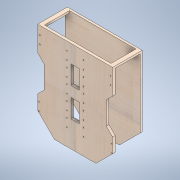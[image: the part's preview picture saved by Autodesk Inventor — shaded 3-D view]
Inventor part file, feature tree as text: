
AUTODESK INVENTOR PART (.ipt)
format: ipt  version: 2021 (Build 250183000, 183)  size: 348,672 bytes
history: native  units: mm
features: extrude x11, sketch x11, other x1, chamfer x1
ambient origin geometry x8: Origin, YZ Plane, XZ Plane, XY Plane, X Axis, Y Axis, Z Axis, Center Point
bodies: Body1 (feature_tree), Body2 (feature_tree)
feature tree (24):
  other  "Sólido1"
  extrude  "Extrusión1"  Depth=120.0mm
  extrude  "Extrusión2"  Depth=180.0mm
  extrude  "Extrusión3"  Depth=100.0mm
  extrude  "Extrusión4"  Depth=12.55mm TaperAngle=0.0deg
  extrude  "Extrusión6"  Depth=30.0mm
  extrude  "Extrusión7"  Depth=30.0mm
  extrude  "Extrusión8"  Depth=10.0mm
  extrude  "Extrusión9"  Depth=5.0mm
  extrude  "Extrusión10"  Depth=19.5mm
  extrude  "Extrusión11"  Depth=40.0mm
  chamfer  "Chaflán1"  Distance=19.5mm
  extrude  "Extrusión12"  Depth=125.0mm
  sketch  "Boceto1"  dims[d0=120.0mm d1=70.0mm]
  sketch  "Boceto2"  dims[d2=110.0mm d3=180.0mm]
  sketch  "Boceto3"  dims[d8=100.0mm d9=80.0mm]
  sketch  "Boceto4"  dims[d13=150.0mm d14=12.55mm d15=0.0mm]
  sketch  "Boceto6"  dims[d17=80.0mm d18=30.0mm]
  sketch  "Boceto7"  dims[d19=30.0mm d20=60.0mm]
  sketch  "Boceto8"  dims[d22=30.0mm d23=10.0mm]
  sketch  "Boceto9"  dims[d25=39.0mm d26=5.0mm]
  sketch  "Boceto10"  dims[d27=14.75mm d28=0.0mm d29=19.5mm]
  sketch  "Boceto11"  dims[d30=70.0mm d31=40.0mm]
  sketch  "Boceto12"  dims[d32=80.0mm d33=19.5mm d34=5.0mm d35=14.75mm d36=0.0mm d37=70.0mm d38=70.0mm d39=35.0mm d40=5.0mm d41=39.0mm d42=5.0mm d43=5.0mm d44=14.75mm d45=0.0mm d46=70.0mm d56=40.0mm d57=25.0mm d58=25.0mm d59=14.75mm d60=0.0mm d63=25.0mm d64=40.0mm d65=25.0mm d66=40.0mm d67=14.75mm d68=0.0mm d69=20.0mm d70=45.0mm d71=90.0mm d72=10.0mm d73=10.0mm d74=10.0mm d75=10.0mm d76=10.0mm d77=10.0mm d78=85.0mm d79=10.0mm d80=10.0mm d81=10.0mm d82=85.0mm d83=10.0mm d84=10.0mm d85=10.0mm d86=7.0mm d87=0.0mm d88=10.0mm d89=20.0mm d90=10.0mm d91=20.0mm d92=130.0mm d93=0.0mm d94=10.0mm d95=10.0mm d96=320.0mm d97=0.0mm d98=430.0mm d99=0.0mm d100=100.0mm d101=2.0mm d102=45.0deg d103=20.0mm d104=40.0mm d105=15.0mm d106=40.0mm d107=125.0mm d108=0.0mm]
